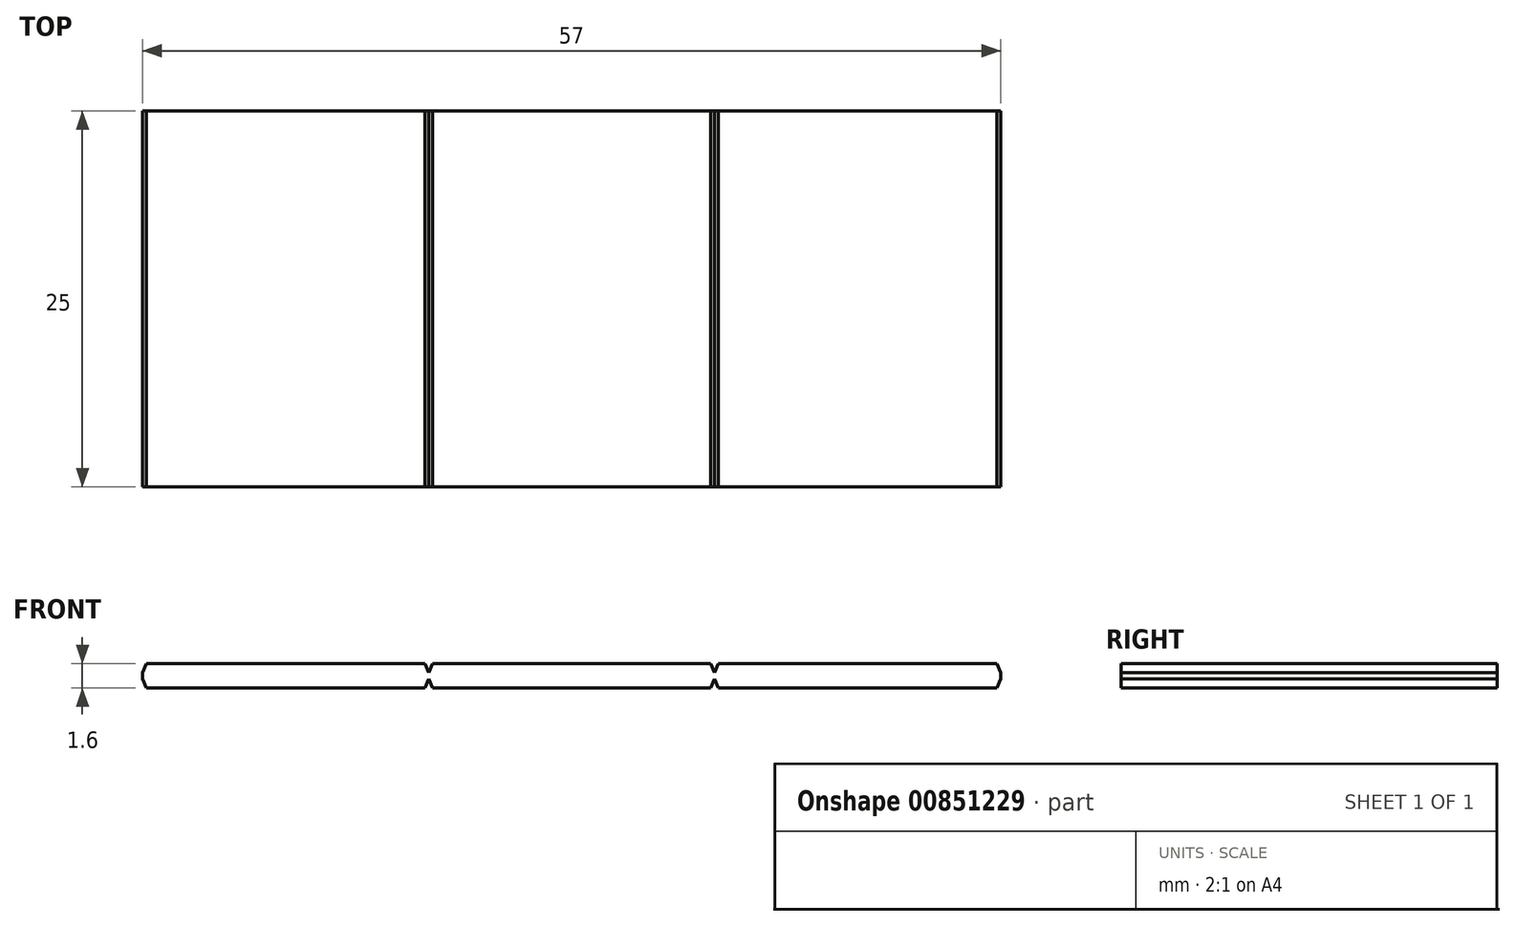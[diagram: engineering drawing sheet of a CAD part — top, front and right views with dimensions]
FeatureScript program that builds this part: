
annotation { "Feature Type Name" : "Feature", "Feature Type Description" : "" }
export const myFeature = defineFeature(function(context is Context, id is Id, definition is map)
    precondition{}
    {
        {
            var Q0;
            Q0=qCreatedBy(makeId("Front.planeOp"),FACE);
            var sketch = newSketch(context, id + "F0", { "sketchPlane" : qUnion([Q0])});
            skLineSegment(sketch, "E0", {"start": v(0, 0.8) * mm, "end": v(-9.25, 0.8) * mm});
            skLineSegment(sketch, "E1", {"start": v(-9.25, 0.8) * mm, "end": v(-9.5, 0.2) * mm});
            skLineSegment(sketch, "E2.MirrorCS", {"start": v(9.25, 0.8) * mm, "end": v(9.5, 0.2) * mm});
            skLineSegment(sketch, "E3.MirrorCS", {"start": v(0, 0.8) * mm, "end": v(9.25, 0.8) * mm});
            skLineSegment(sketch, "E4.MirrorCS", {"start": v(0, -0.8) * mm, "end": v(9.25, -0.8) * mm});
            skLineSegment(sketch, "E5.MirrorCS", {"start": v(-9.25, -0.8) * mm, "end": v(-9.5, -0.2) * mm});
            skLineSegment(sketch, "E6.MirrorCS", {"start": v(0, -0.8) * mm, "end": v(-9.25, -0.8) * mm});
            skLineSegment(sketch, "E7.MirrorCS", {"start": v(9.25, -0.8) * mm, "end": v(9.5, -0.2) * mm});
            skLineSegment(sketch, "E8.1.0.0", {"start": v(19, 0.8) * mm, "end": v(9.75, 0.8) * mm});
            skLineSegment(sketch, "E8.1.0.1", {"start": v(28.25, -0.8) * mm, "end": v(28.5, -0.2) * mm});
            skLineSegment(sketch, "E8.1.0.2", {"start": v(28.25, 0.8) * mm, "end": v(28.5, 0.2) * mm});
            skLineSegment(sketch, "E8.1.0.3", {"start": v(19, -0.8) * mm, "end": v(9.75, -0.8) * mm});
            skLineSegment(sketch, "E8.1.0.4", {"start": v(9.75, 0.8) * mm, "end": v(9.5, 0.2) * mm});
            skLineSegment(sketch, "E8.1.0.5", {"start": v(19, 0.8) * mm, "end": v(28.25, 0.8) * mm});
            skLineSegment(sketch, "E8.1.0.6", {"start": v(9.75, -0.8) * mm, "end": v(9.5, -0.2) * mm});
            skLineSegment(sketch, "E8.1.0.7", {"start": v(19, -0.8) * mm, "end": v(28.25, -0.8) * mm});
            skLineSegment(sketch, "E8.1.0.8", {"start": v(19, 0.8) * mm, "end": v(9.75, 0.8) * mm});
            skLineSegment(sketch, "E8.1.0.9", {"start": v(19, -0.8) * mm, "end": v(28.25, -0.8) * mm});
            skLineSegment(sketch, "E8.1.0.10", {"start": v(28.25, -0.8) * mm, "end": v(28.5, -0.2) * mm});
            skLineSegment(sketch, "E8.1.0.11", {"start": v(9.75, 0.8) * mm, "end": v(9.5, 0.2) * mm});
            skLineSegment(sketch, "E8.1.0.12", {"start": v(19, 0.8) * mm, "end": v(28.25, 0.8) * mm});
            skLineSegment(sketch, "E8.1.0.13", {"start": v(28.25, 0.8) * mm, "end": v(28.5, 0.2) * mm});
            skLineSegment(sketch, "E8.1.0.14", {"start": v(19, -0.8) * mm, "end": v(9.75, -0.8) * mm});
            skLineSegment(sketch, "E8.1.0.15", {"start": v(9.75, -0.8) * mm, "end": v(9.5, -0.2) * mm});
            skLineSegment(sketch, "E8.1.0.16", {"start": v(19, 0.8) * mm, "end": v(9.75, 0.8) * mm});
            skLineSegment(sketch, "E8.1.0.17", {"start": v(9.75, 0.8) * mm, "end": v(9.5, 0.2) * mm});
            skLineSegment(sketch, "E8.1.0.18", {"start": v(28.25, -0.8) * mm, "end": v(28.5, -0.2) * mm});
            skLineSegment(sketch, "E8.1.0.19", {"start": v(19, -0.8) * mm, "end": v(28.25, -0.8) * mm});
            skLineSegment(sketch, "E8.1.0.20", {"start": v(19, -0.8) * mm, "end": v(9.75, -0.8) * mm});
            skLineSegment(sketch, "E8.1.0.21", {"start": v(19, 0.8) * mm, "end": v(28.25, 0.8) * mm});
            skLineSegment(sketch, "E8.1.0.22", {"start": v(28.25, 0.8) * mm, "end": v(28.5, 0.2) * mm});
            skLineSegment(sketch, "E8.1.0.23", {"start": v(9.75, -0.8) * mm, "end": v(9.5, -0.2) * mm});
            skLineSegment(sketch, "E8.1.0.24", {"start": v(19, 0.8) * mm, "end": v(9.75, 0.8) * mm});
            skLineSegment(sketch, "E8.1.0.25", {"start": v(9.75, 0.8) * mm, "end": v(9.5, 0.2) * mm});
            skLineSegment(sketch, "E8.1.0.26", {"start": v(28.25, -0.8) * mm, "end": v(28.5, -0.2) * mm});
            skLineSegment(sketch, "E8.1.0.27", {"start": v(19, -0.8) * mm, "end": v(9.75, -0.8) * mm});
            skLineSegment(sketch, "E8.1.0.28", {"start": v(19, 0.8) * mm, "end": v(28.25, 0.8) * mm});
            skLineSegment(sketch, "E8.1.0.29", {"start": v(19, -0.8) * mm, "end": v(28.25, -0.8) * mm});
            skLineSegment(sketch, "E8.1.0.30", {"start": v(28.25, 0.8) * mm, "end": v(28.5, 0.2) * mm});
            skLineSegment(sketch, "E8.1.0.31", {"start": v(9.75, -0.8) * mm, "end": v(9.5, -0.2) * mm});
            skLineSegment(sketch, "E8.1.0.32", {"start": v(19, 0.8) * mm, "end": v(9.75, 0.8) * mm});
            skLineSegment(sketch, "E8.1.0.33", {"start": v(9.75, 0.8) * mm, "end": v(9.5, 0.2) * mm});
            skLineSegment(sketch, "E8.1.0.34", {"start": v(19, 0.8) * mm, "end": v(28.25, 0.8) * mm});
            skLineSegment(sketch, "E8.1.0.35", {"start": v(19, -0.8) * mm, "end": v(9.75, -0.8) * mm});
            skLineSegment(sketch, "E8.1.0.36", {"start": v(28.25, -0.8) * mm, "end": v(28.5, -0.2) * mm});
            skLineSegment(sketch, "E8.1.0.37", {"start": v(19, -0.8) * mm, "end": v(28.25, -0.8) * mm});
            skLineSegment(sketch, "E8.1.0.38", {"start": v(28.25, 0.8) * mm, "end": v(28.5, 0.2) * mm});
            skLineSegment(sketch, "E8.1.0.39", {"start": v(9.75, -0.8) * mm, "end": v(9.5, -0.2) * mm});
            skLineSegment(sketch, "E8.1.0.40", {"start": v(19, -0.8) * mm, "end": v(28.25, -0.8) * mm});
            skLineSegment(sketch, "E8.1.0.41", {"start": v(19, 0.8) * mm, "end": v(9.75, 0.8) * mm});
            skLineSegment(sketch, "E8.1.0.42", {"start": v(19, -0.8) * mm, "end": v(9.75, -0.8) * mm});
            skLineSegment(sketch, "E8.1.0.43", {"start": v(9.75, 0.8) * mm, "end": v(9.5, 0.2) * mm});
            skLineSegment(sketch, "E8.1.0.44", {"start": v(19, 0.8) * mm, "end": v(28.25, 0.8) * mm});
            skLineSegment(sketch, "E8.1.0.45", {"start": v(28.25, -0.8) * mm, "end": v(28.5, -0.2) * mm});
            skLineSegment(sketch, "E8.1.0.46", {"start": v(9.75, -0.8) * mm, "end": v(9.5, -0.2) * mm});
            skLineSegment(sketch, "E8.1.0.47", {"start": v(28.25, 0.8) * mm, "end": v(28.5, 0.2) * mm});
            skLineSegment(sketch, "E8.1.0.48", {"start": v(19, -0.8) * mm, "end": v(28.25, -0.8) * mm});
            skLineSegment(sketch, "E8.1.0.49", {"start": v(19, 0.8) * mm, "end": v(9.75, 0.8) * mm});
            skLineSegment(sketch, "E8.1.0.50", {"start": v(19, -0.8) * mm, "end": v(9.75, -0.8) * mm});
            skLineSegment(sketch, "E8.1.0.51", {"start": v(28.25, -0.8) * mm, "end": v(28.5, -0.2) * mm});
            skLineSegment(sketch, "E8.1.0.52", {"start": v(9.75, 0.8) * mm, "end": v(9.5, 0.2) * mm});
            skLineSegment(sketch, "E8.1.0.53", {"start": v(9.75, -0.8) * mm, "end": v(9.5, -0.2) * mm});
            skLineSegment(sketch, "E8.1.0.54", {"start": v(19, 0.8) * mm, "end": v(28.25, 0.8) * mm});
            skLineSegment(sketch, "E8.1.0.55", {"start": v(28.25, 0.8) * mm, "end": v(28.5, 0.2) * mm});
            skLineSegment(sketch, "E8.1.0.56", {"start": v(28.25, -0.8) * mm, "end": v(28.5, -0.2) * mm});
            skLineSegment(sketch, "E8.1.0.57", {"start": v(19, -0.8) * mm, "end": v(28.25, -0.8) * mm});
            skLineSegment(sketch, "E8.1.0.58", {"start": v(19, -0.8) * mm, "end": v(9.75, -0.8) * mm});
            skLineSegment(sketch, "E8.1.0.59", {"start": v(19, 0.8) * mm, "end": v(9.75, 0.8) * mm});
            skLineSegment(sketch, "E8.1.0.60", {"start": v(19, 0.8) * mm, "end": v(28.25, 0.8) * mm});
            skLineSegment(sketch, "E8.1.0.61", {"start": v(9.75, 0.8) * mm, "end": v(9.5, 0.2) * mm});
            skLineSegment(sketch, "E8.1.0.62", {"start": v(9.75, -0.8) * mm, "end": v(9.5, -0.2) * mm});
            skLineSegment(sketch, "E8.1.0.63", {"start": v(28.25, 0.8) * mm, "end": v(28.5, 0.2) * mm});
            skLineSegment(sketch, "E8.1.0.64", {"start": v(19, -0.8) * mm, "end": v(28.25, -0.8) * mm});
            skLineSegment(sketch, "E8.1.0.65", {"start": v(19, 0.8) * mm, "end": v(9.75, 0.8) * mm});
            skLineSegment(sketch, "E8.1.0.66", {"start": v(19, -0.8) * mm, "end": v(9.75, -0.8) * mm});
            skLineSegment(sketch, "E8.1.0.67", {"start": v(28.25, 0.8) * mm, "end": v(28.5, 0.2) * mm});
            skLineSegment(sketch, "E8.1.0.68", {"start": v(28.25, -0.8) * mm, "end": v(28.5, -0.2) * mm});
            skLineSegment(sketch, "E8.1.0.69", {"start": v(19, 0.8) * mm, "end": v(28.25, 0.8) * mm});
            skLineSegment(sketch, "E8.1.0.70", {"start": v(9.75, 0.8) * mm, "end": v(9.5, 0.2) * mm});
            skLineSegment(sketch, "E8.1.0.71", {"start": v(9.75, -0.8) * mm, "end": v(9.5, -0.2) * mm});
            skLineSegment(sketch, "E8.1.0.72", {"start": v(19, -0.8) * mm, "end": v(28.25, -0.8) * mm});
            skLineSegment(sketch, "E8.1.0.73", {"start": v(28.25, -0.8) * mm, "end": v(28.5, -0.2) * mm});
            skLineSegment(sketch, "E8.1.0.74", {"start": v(19, -0.8) * mm, "end": v(9.75, -0.8) * mm});
            skLineSegment(sketch, "E8.1.0.75", {"start": v(9.75, 0.8) * mm, "end": v(9.5, 0.2) * mm});
            skLineSegment(sketch, "E8.1.0.76", {"start": v(19, 0.8) * mm, "end": v(9.75, 0.8) * mm});
            skLineSegment(sketch, "E8.1.0.77", {"start": v(28.25, 0.8) * mm, "end": v(28.5, 0.2) * mm});
            skLineSegment(sketch, "E8.1.0.78", {"start": v(19, 0.8) * mm, "end": v(28.25, 0.8) * mm});
            skLineSegment(sketch, "E8.1.0.79", {"start": v(9.75, -0.8) * mm, "end": v(9.5, -0.2) * mm});
            skLineSegment(sketch, "E8.1.0.80", {"start": v(9.75, 0.8) * mm, "end": v(9.5, 0.2) * mm});
            skLineSegment(sketch, "E8.1.0.81", {"start": v(19, 0.8) * mm, "end": v(28.25, 0.8) * mm});
            skLineSegment(sketch, "E8.1.0.82", {"start": v(9.75, -0.8) * mm, "end": v(9.5, -0.2) * mm});
            skLineSegment(sketch, "E8.1.0.83", {"start": v(28.25, -0.8) * mm, "end": v(28.5, -0.2) * mm});
            skLineSegment(sketch, "E8.1.0.84", {"start": v(19, -0.8) * mm, "end": v(9.75, -0.8) * mm});
            skLineSegment(sketch, "E8.1.0.85", {"start": v(19, -0.8) * mm, "end": v(28.25, -0.8) * mm});
            skLineSegment(sketch, "E8.1.0.86", {"start": v(19, 0.8) * mm, "end": v(9.75, 0.8) * mm});
            skLineSegment(sketch, "E8.1.0.87", {"start": v(28.25, 0.8) * mm, "end": v(28.5, 0.2) * mm});
            skLineSegment(sketch, "E8.1.0.88", {"start": v(9.75, 0.8) * mm, "end": v(9.5, 0.2) * mm});
            skLineSegment(sketch, "E8.1.0.89", {"start": v(9.75, -0.8) * mm, "end": v(9.5, -0.2) * mm});
            skLineSegment(sketch, "E8.1.0.90", {"start": v(19, -0.8) * mm, "end": v(28.25, -0.8) * mm});
            skLineSegment(sketch, "E8.1.0.91", {"start": v(28.25, 0.8) * mm, "end": v(28.5, 0.2) * mm});
            skLineSegment(sketch, "E8.1.0.92", {"start": v(19, 0.8) * mm, "end": v(9.75, 0.8) * mm});
            skLineSegment(sketch, "E8.1.0.93", {"start": v(19, -0.8) * mm, "end": v(9.75, -0.8) * mm});
            skLineSegment(sketch, "E8.1.0.94", {"start": v(19, 0.8) * mm, "end": v(28.25, 0.8) * mm});
            skLineSegment(sketch, "E8.1.0.95", {"start": v(28.25, -0.8) * mm, "end": v(28.5, -0.2) * mm});
            skLineSegment(sketch, "E8.1.0.96", {"start": v(28.25, 0.8) * mm, "end": v(28.5, 0.2) * mm});
            skLineSegment(sketch, "E8.1.0.97", {"start": v(19, -0.8) * mm, "end": v(28.25, -0.8) * mm});
            skLineSegment(sketch, "E8.1.0.98", {"start": v(9.75, 0.8) * mm, "end": v(9.5, 0.2) * mm});
            skLineSegment(sketch, "E8.1.0.99", {"start": v(19, 0.8) * mm, "end": v(9.75, 0.8) * mm});
            skLineSegment(sketch, "E8.1.0.100", {"start": v(19, -0.8) * mm, "end": v(9.75, -0.8) * mm});
            skLineSegment(sketch, "E8.1.0.101", {"start": v(19, 0.8) * mm, "end": v(28.25, 0.8) * mm});
            skLineSegment(sketch, "E8.1.0.102", {"start": v(28.25, -0.8) * mm, "end": v(28.5, -0.2) * mm});
            skLineSegment(sketch, "E8.1.0.103", {"start": v(9.75, -0.8) * mm, "end": v(9.5, -0.2) * mm});
            skLineSegment(sketch, "E8.1.0.104", {"start": v(19, -0.8) * mm, "end": v(9.75, -0.8) * mm});
            skLineSegment(sketch, "E8.1.0.105", {"start": v(19, 0.8) * mm, "end": v(28.25, 0.8) * mm});
            skLineSegment(sketch, "E8.1.0.106", {"start": v(28.25, 0.8) * mm, "end": v(28.5, 0.2) * mm});
            skLineSegment(sketch, "E8.1.0.107", {"start": v(28.25, -0.8) * mm, "end": v(28.5, -0.2) * mm});
            skLineSegment(sketch, "E8.1.0.108", {"start": v(9.75, -0.8) * mm, "end": v(9.5, -0.2) * mm});
            skLineSegment(sketch, "E8.1.0.109", {"start": v(9.75, 0.8) * mm, "end": v(9.5, 0.2) * mm});
            skLineSegment(sketch, "E8.1.0.110", {"start": v(19, 0.8) * mm, "end": v(9.75, 0.8) * mm});
            skLineSegment(sketch, "E8.1.0.111", {"start": v(19, -0.8) * mm, "end": v(28.25, -0.8) * mm});
            skLineSegment(sketch, "E8.1.0.112", {"start": v(28.25, -0.8) * mm, "end": v(28.5, -0.2) * mm});
            skLineSegment(sketch, "E8.1.0.113", {"start": v(19, 0.8) * mm, "end": v(28.25, 0.8) * mm});
            skLineSegment(sketch, "E8.1.0.114", {"start": v(28.25, 0.8) * mm, "end": v(28.5, 0.2) * mm});
            skLineSegment(sketch, "E8.1.0.115", {"start": v(9.75, -0.8) * mm, "end": v(9.5, -0.2) * mm});
            skLineSegment(sketch, "E8.1.0.116", {"start": v(9.75, 0.8) * mm, "end": v(9.5, 0.2) * mm});
            skLineSegment(sketch, "E8.1.0.117", {"start": v(19, -0.8) * mm, "end": v(9.75, -0.8) * mm});
            skLineSegment(sketch, "E8.1.0.118", {"start": v(19, -0.8) * mm, "end": v(28.25, -0.8) * mm});
            skLineSegment(sketch, "E8.1.0.119", {"start": v(19, 0.8) * mm, "end": v(9.75, 0.8) * mm});
            skLineSegment(sketch, "E8.1.0.120", {"start": v(28.25, 0.8) * mm, "end": v(28.5, 0.2) * mm});
            skLineSegment(sketch, "E8.1.0.121", {"start": v(9.75, -0.8) * mm, "end": v(9.5, -0.2) * mm});
            skLineSegment(sketch, "E8.1.0.122", {"start": v(19, 0.8) * mm, "end": v(9.75, 0.8) * mm});
            skLineSegment(sketch, "E8.1.0.123", {"start": v(19, -0.8) * mm, "end": v(28.25, -0.8) * mm});
            skLineSegment(sketch, "E8.1.0.124", {"start": v(19, -0.8) * mm, "end": v(9.75, -0.8) * mm});
            skLineSegment(sketch, "E8.1.0.125", {"start": v(19, 0.8) * mm, "end": v(28.25, 0.8) * mm});
            skLineSegment(sketch, "E8.1.0.126", {"start": v(9.75, 0.8) * mm, "end": v(9.5, 0.2) * mm});
            skLineSegment(sketch, "E8.1.0.127", {"start": v(28.25, -0.8) * mm, "end": v(28.5, -0.2) * mm});
            skLineSegment(sketch, "E8.2.0.0", {"start": v(38, 0.8) * mm, "end": v(28.75, 0.8) * mm});
            skLineSegment(sketch, "E8.2.0.1", {"start": v(47.25, -0.8) * mm, "end": v(47.5, -0.2) * mm});
            skLineSegment(sketch, "E8.2.0.2", {"start": v(47.25, 0.8) * mm, "end": v(47.5, 0.2) * mm});
            skLineSegment(sketch, "E8.2.0.3", {"start": v(38, -0.8) * mm, "end": v(28.75, -0.8) * mm});
            skLineSegment(sketch, "E8.2.0.4", {"start": v(28.75, 0.8) * mm, "end": v(28.5, 0.2) * mm});
            skLineSegment(sketch, "E8.2.0.5", {"start": v(38, 0.8) * mm, "end": v(47.25, 0.8) * mm});
            skLineSegment(sketch, "E8.2.0.6", {"start": v(28.75, -0.8) * mm, "end": v(28.5, -0.2) * mm});
            skLineSegment(sketch, "E8.2.0.7", {"start": v(38, -0.8) * mm, "end": v(47.25, -0.8) * mm});
            skLineSegment(sketch, "E8.2.0.8", {"start": v(38, 0.8) * mm, "end": v(28.75, 0.8) * mm});
            skLineSegment(sketch, "E8.2.0.9", {"start": v(38, -0.8) * mm, "end": v(47.25, -0.8) * mm});
            skLineSegment(sketch, "E8.2.0.10", {"start": v(47.25, -0.8) * mm, "end": v(47.5, -0.2) * mm});
            skLineSegment(sketch, "E8.2.0.11", {"start": v(28.75, 0.8) * mm, "end": v(28.5, 0.2) * mm});
            skLineSegment(sketch, "E8.2.0.12", {"start": v(38, 0.8) * mm, "end": v(47.25, 0.8) * mm});
            skLineSegment(sketch, "E8.2.0.13", {"start": v(47.25, 0.8) * mm, "end": v(47.5, 0.2) * mm});
            skLineSegment(sketch, "E8.2.0.14", {"start": v(38, -0.8) * mm, "end": v(28.75, -0.8) * mm});
            skLineSegment(sketch, "E8.2.0.15", {"start": v(28.75, -0.8) * mm, "end": v(28.5, -0.2) * mm});
            skLineSegment(sketch, "E8.2.0.16", {"start": v(38, 0.8) * mm, "end": v(28.75, 0.8) * mm});
            skLineSegment(sketch, "E8.2.0.17", {"start": v(28.75, 0.8) * mm, "end": v(28.5, 0.2) * mm});
            skLineSegment(sketch, "E8.2.0.18", {"start": v(47.25, -0.8) * mm, "end": v(47.5, -0.2) * mm});
            skLineSegment(sketch, "E8.2.0.19", {"start": v(38, -0.8) * mm, "end": v(47.25, -0.8) * mm});
            skLineSegment(sketch, "E8.2.0.20", {"start": v(38, -0.8) * mm, "end": v(28.75, -0.8) * mm});
            skLineSegment(sketch, "E8.2.0.21", {"start": v(38, 0.8) * mm, "end": v(47.25, 0.8) * mm});
            skLineSegment(sketch, "E8.2.0.22", {"start": v(47.25, 0.8) * mm, "end": v(47.5, 0.2) * mm});
            skLineSegment(sketch, "E8.2.0.23", {"start": v(28.75, -0.8) * mm, "end": v(28.5, -0.2) * mm});
            skLineSegment(sketch, "E8.2.0.24", {"start": v(38, 0.8) * mm, "end": v(28.75, 0.8) * mm});
            skLineSegment(sketch, "E8.2.0.25", {"start": v(28.75, 0.8) * mm, "end": v(28.5, 0.2) * mm});
            skLineSegment(sketch, "E8.2.0.26", {"start": v(47.25, -0.8) * mm, "end": v(47.5, -0.2) * mm});
            skLineSegment(sketch, "E8.2.0.27", {"start": v(38, -0.8) * mm, "end": v(28.75, -0.8) * mm});
            skLineSegment(sketch, "E8.2.0.28", {"start": v(38, 0.8) * mm, "end": v(47.25, 0.8) * mm});
            skLineSegment(sketch, "E8.2.0.29", {"start": v(38, -0.8) * mm, "end": v(47.25, -0.8) * mm});
            skLineSegment(sketch, "E8.2.0.30", {"start": v(47.25, 0.8) * mm, "end": v(47.5, 0.2) * mm});
            skLineSegment(sketch, "E8.2.0.31", {"start": v(28.75, -0.8) * mm, "end": v(28.5, -0.2) * mm});
            skLineSegment(sketch, "E8.2.0.32", {"start": v(38, 0.8) * mm, "end": v(28.75, 0.8) * mm});
            skLineSegment(sketch, "E8.2.0.33", {"start": v(28.75, 0.8) * mm, "end": v(28.5, 0.2) * mm});
            skLineSegment(sketch, "E8.2.0.34", {"start": v(38, 0.8) * mm, "end": v(47.25, 0.8) * mm});
            skLineSegment(sketch, "E8.2.0.35", {"start": v(38, -0.8) * mm, "end": v(28.75, -0.8) * mm});
            skLineSegment(sketch, "E8.2.0.36", {"start": v(47.25, -0.8) * mm, "end": v(47.5, -0.2) * mm});
            skLineSegment(sketch, "E8.2.0.37", {"start": v(38, -0.8) * mm, "end": v(47.25, -0.8) * mm});
            skLineSegment(sketch, "E8.2.0.38", {"start": v(47.25, 0.8) * mm, "end": v(47.5, 0.2) * mm});
            skLineSegment(sketch, "E8.2.0.39", {"start": v(28.75, -0.8) * mm, "end": v(28.5, -0.2) * mm});
            skLineSegment(sketch, "E8.2.0.40", {"start": v(38, -0.8) * mm, "end": v(47.25, -0.8) * mm});
            skLineSegment(sketch, "E8.2.0.41", {"start": v(38, 0.8) * mm, "end": v(28.75, 0.8) * mm});
            skLineSegment(sketch, "E8.2.0.42", {"start": v(38, -0.8) * mm, "end": v(28.75, -0.8) * mm});
            skLineSegment(sketch, "E8.2.0.43", {"start": v(28.75, 0.8) * mm, "end": v(28.5, 0.2) * mm});
            skLineSegment(sketch, "E8.2.0.44", {"start": v(38, 0.8) * mm, "end": v(47.25, 0.8) * mm});
            skLineSegment(sketch, "E8.2.0.45", {"start": v(47.25, -0.8) * mm, "end": v(47.5, -0.2) * mm});
            skLineSegment(sketch, "E8.2.0.46", {"start": v(28.75, -0.8) * mm, "end": v(28.5, -0.2) * mm});
            skLineSegment(sketch, "E8.2.0.47", {"start": v(47.25, 0.8) * mm, "end": v(47.5, 0.2) * mm});
            skLineSegment(sketch, "E8.2.0.48", {"start": v(38, -0.8) * mm, "end": v(47.25, -0.8) * mm});
            skLineSegment(sketch, "E8.2.0.49", {"start": v(38, 0.8) * mm, "end": v(28.75, 0.8) * mm});
            skLineSegment(sketch, "E8.2.0.50", {"start": v(38, -0.8) * mm, "end": v(28.75, -0.8) * mm});
            skLineSegment(sketch, "E8.2.0.51", {"start": v(47.25, -0.8) * mm, "end": v(47.5, -0.2) * mm});
            skLineSegment(sketch, "E8.2.0.52", {"start": v(28.75, 0.8) * mm, "end": v(28.5, 0.2) * mm});
            skLineSegment(sketch, "E8.2.0.53", {"start": v(28.75, -0.8) * mm, "end": v(28.5, -0.2) * mm});
            skLineSegment(sketch, "E8.2.0.54", {"start": v(38, 0.8) * mm, "end": v(47.25, 0.8) * mm});
            skLineSegment(sketch, "E8.2.0.55", {"start": v(47.25, 0.8) * mm, "end": v(47.5, 0.2) * mm});
            skLineSegment(sketch, "E8.2.0.56", {"start": v(47.25, -0.8) * mm, "end": v(47.5, -0.2) * mm});
            skLineSegment(sketch, "E8.2.0.57", {"start": v(38, -0.8) * mm, "end": v(47.25, -0.8) * mm});
            skLineSegment(sketch, "E8.2.0.58", {"start": v(38, -0.8) * mm, "end": v(28.75, -0.8) * mm});
            skLineSegment(sketch, "E8.2.0.59", {"start": v(38, 0.8) * mm, "end": v(28.75, 0.8) * mm});
            skLineSegment(sketch, "E8.2.0.60", {"start": v(38, 0.8) * mm, "end": v(47.25, 0.8) * mm});
            skLineSegment(sketch, "E8.2.0.61", {"start": v(28.75, 0.8) * mm, "end": v(28.5, 0.2) * mm});
            skLineSegment(sketch, "E8.2.0.62", {"start": v(28.75, -0.8) * mm, "end": v(28.5, -0.2) * mm});
            skLineSegment(sketch, "E8.2.0.63", {"start": v(47.25, 0.8) * mm, "end": v(47.5, 0.2) * mm});
            skLineSegment(sketch, "E8.2.0.64", {"start": v(38, -0.8) * mm, "end": v(47.25, -0.8) * mm});
            skLineSegment(sketch, "E8.2.0.65", {"start": v(38, 0.8) * mm, "end": v(28.75, 0.8) * mm});
            skLineSegment(sketch, "E8.2.0.66", {"start": v(38, -0.8) * mm, "end": v(28.75, -0.8) * mm});
            skLineSegment(sketch, "E8.2.0.67", {"start": v(47.25, 0.8) * mm, "end": v(47.5, 0.2) * mm});
            skLineSegment(sketch, "E8.2.0.68", {"start": v(47.25, -0.8) * mm, "end": v(47.5, -0.2) * mm});
            skLineSegment(sketch, "E8.2.0.69", {"start": v(38, 0.8) * mm, "end": v(47.25, 0.8) * mm});
            skLineSegment(sketch, "E8.2.0.70", {"start": v(28.75, 0.8) * mm, "end": v(28.5, 0.2) * mm});
            skLineSegment(sketch, "E8.2.0.71", {"start": v(28.75, -0.8) * mm, "end": v(28.5, -0.2) * mm});
            skLineSegment(sketch, "E8.2.0.72", {"start": v(38, -0.8) * mm, "end": v(47.25, -0.8) * mm});
            skLineSegment(sketch, "E8.2.0.73", {"start": v(47.25, -0.8) * mm, "end": v(47.5, -0.2) * mm});
            skLineSegment(sketch, "E8.2.0.74", {"start": v(38, -0.8) * mm, "end": v(28.75, -0.8) * mm});
            skLineSegment(sketch, "E8.2.0.75", {"start": v(28.75, 0.8) * mm, "end": v(28.5, 0.2) * mm});
            skLineSegment(sketch, "E8.2.0.76", {"start": v(38, 0.8) * mm, "end": v(28.75, 0.8) * mm});
            skLineSegment(sketch, "E8.2.0.77", {"start": v(47.25, 0.8) * mm, "end": v(47.5, 0.2) * mm});
            skLineSegment(sketch, "E8.2.0.78", {"start": v(38, 0.8) * mm, "end": v(47.25, 0.8) * mm});
            skLineSegment(sketch, "E8.2.0.79", {"start": v(28.75, -0.8) * mm, "end": v(28.5, -0.2) * mm});
            skLineSegment(sketch, "E8.2.0.80", {"start": v(28.75, 0.8) * mm, "end": v(28.5, 0.2) * mm});
            skLineSegment(sketch, "E8.2.0.81", {"start": v(38, 0.8) * mm, "end": v(47.25, 0.8) * mm});
            skLineSegment(sketch, "E8.2.0.82", {"start": v(28.75, -0.8) * mm, "end": v(28.5, -0.2) * mm});
            skLineSegment(sketch, "E8.2.0.83", {"start": v(47.25, -0.8) * mm, "end": v(47.5, -0.2) * mm});
            skLineSegment(sketch, "E8.2.0.84", {"start": v(38, -0.8) * mm, "end": v(28.75, -0.8) * mm});
            skLineSegment(sketch, "E8.2.0.85", {"start": v(38, -0.8) * mm, "end": v(47.25, -0.8) * mm});
            skLineSegment(sketch, "E8.2.0.86", {"start": v(38, 0.8) * mm, "end": v(28.75, 0.8) * mm});
            skLineSegment(sketch, "E8.2.0.87", {"start": v(47.25, 0.8) * mm, "end": v(47.5, 0.2) * mm});
            skLineSegment(sketch, "E8.2.0.88", {"start": v(28.75, 0.8) * mm, "end": v(28.5, 0.2) * mm});
            skLineSegment(sketch, "E8.2.0.89", {"start": v(28.75, -0.8) * mm, "end": v(28.5, -0.2) * mm});
            skLineSegment(sketch, "E8.2.0.90", {"start": v(38, -0.8) * mm, "end": v(47.25, -0.8) * mm});
            skLineSegment(sketch, "E8.2.0.91", {"start": v(47.25, 0.8) * mm, "end": v(47.5, 0.2) * mm});
            skLineSegment(sketch, "E8.2.0.92", {"start": v(38, 0.8) * mm, "end": v(28.75, 0.8) * mm});
            skLineSegment(sketch, "E8.2.0.93", {"start": v(38, -0.8) * mm, "end": v(28.75, -0.8) * mm});
            skLineSegment(sketch, "E8.2.0.94", {"start": v(38, 0.8) * mm, "end": v(47.25, 0.8) * mm});
            skLineSegment(sketch, "E8.2.0.95", {"start": v(47.25, -0.8) * mm, "end": v(47.5, -0.2) * mm});
            skLineSegment(sketch, "E8.2.0.96", {"start": v(47.25, 0.8) * mm, "end": v(47.5, 0.2) * mm});
            skLineSegment(sketch, "E8.2.0.97", {"start": v(38, -0.8) * mm, "end": v(47.25, -0.8) * mm});
            skLineSegment(sketch, "E8.2.0.98", {"start": v(28.75, 0.8) * mm, "end": v(28.5, 0.2) * mm});
            skLineSegment(sketch, "E8.2.0.99", {"start": v(38, 0.8) * mm, "end": v(28.75, 0.8) * mm});
            skLineSegment(sketch, "E8.2.0.100", {"start": v(38, -0.8) * mm, "end": v(28.75, -0.8) * mm});
            skLineSegment(sketch, "E8.2.0.101", {"start": v(38, 0.8) * mm, "end": v(47.25, 0.8) * mm});
            skLineSegment(sketch, "E8.2.0.102", {"start": v(47.25, -0.8) * mm, "end": v(47.5, -0.2) * mm});
            skLineSegment(sketch, "E8.2.0.103", {"start": v(28.75, -0.8) * mm, "end": v(28.5, -0.2) * mm});
            skLineSegment(sketch, "E8.2.0.104", {"start": v(38, -0.8) * mm, "end": v(28.75, -0.8) * mm});
            skLineSegment(sketch, "E8.2.0.105", {"start": v(38, 0.8) * mm, "end": v(47.25, 0.8) * mm});
            skLineSegment(sketch, "E8.2.0.106", {"start": v(47.25, 0.8) * mm, "end": v(47.5, 0.2) * mm});
            skLineSegment(sketch, "E8.2.0.107", {"start": v(47.25, -0.8) * mm, "end": v(47.5, -0.2) * mm});
            skLineSegment(sketch, "E8.2.0.108", {"start": v(28.75, -0.8) * mm, "end": v(28.5, -0.2) * mm});
            skLineSegment(sketch, "E8.2.0.109", {"start": v(28.75, 0.8) * mm, "end": v(28.5, 0.2) * mm});
            skLineSegment(sketch, "E8.2.0.110", {"start": v(38, 0.8) * mm, "end": v(28.75, 0.8) * mm});
            skLineSegment(sketch, "E8.2.0.111", {"start": v(38, -0.8) * mm, "end": v(47.25, -0.8) * mm});
            skLineSegment(sketch, "E8.2.0.112", {"start": v(47.25, -0.8) * mm, "end": v(47.5, -0.2) * mm});
            skLineSegment(sketch, "E8.2.0.113", {"start": v(38, 0.8) * mm, "end": v(47.25, 0.8) * mm});
            skLineSegment(sketch, "E8.2.0.114", {"start": v(47.25, 0.8) * mm, "end": v(47.5, 0.2) * mm});
            skLineSegment(sketch, "E8.2.0.115", {"start": v(28.75, -0.8) * mm, "end": v(28.5, -0.2) * mm});
            skLineSegment(sketch, "E8.2.0.116", {"start": v(28.75, 0.8) * mm, "end": v(28.5, 0.2) * mm});
            skLineSegment(sketch, "E8.2.0.117", {"start": v(38, -0.8) * mm, "end": v(28.75, -0.8) * mm});
            skLineSegment(sketch, "E8.2.0.118", {"start": v(38, -0.8) * mm, "end": v(47.25, -0.8) * mm});
            skLineSegment(sketch, "E8.2.0.119", {"start": v(38, 0.8) * mm, "end": v(28.75, 0.8) * mm});
            skLineSegment(sketch, "E8.2.0.120", {"start": v(47.25, 0.8) * mm, "end": v(47.5, 0.2) * mm});
            skLineSegment(sketch, "E8.2.0.121", {"start": v(28.75, -0.8) * mm, "end": v(28.5, -0.2) * mm});
            skLineSegment(sketch, "E8.2.0.122", {"start": v(38, 0.8) * mm, "end": v(28.75, 0.8) * mm});
            skLineSegment(sketch, "E8.2.0.123", {"start": v(38, -0.8) * mm, "end": v(47.25, -0.8) * mm});
            skLineSegment(sketch, "E8.2.0.124", {"start": v(38, -0.8) * mm, "end": v(28.75, -0.8) * mm});
            skLineSegment(sketch, "E8.2.0.125", {"start": v(38, 0.8) * mm, "end": v(47.25, 0.8) * mm});
            skLineSegment(sketch, "E8.2.0.126", {"start": v(28.75, 0.8) * mm, "end": v(28.5, 0.2) * mm});
            skLineSegment(sketch, "E8.2.0.127", {"start": v(47.25, -0.8) * mm, "end": v(47.5, -0.2) * mm});
            skLineSegment(sketch, "E8.direction1", {"start": v(-9.25, -0.8) * mm, "end": v(9.75, -0.8) * mm, "construction": true});
            skLineSegment(sketch, "E9", {"start": v(-9.5, 0.2) * mm, "end": v(-9.5, -0.2) * mm});
            skLineSegment(sketch, "E10", {"start": v(47.5, 0.2) * mm, "end": v(47.5, -0.2) * mm});
            skSolve(sketch);
        }
        {
            var Q0;
            Q0=makeQuery(id+"F0.imprint","IMPRINT",FACE,{"disambiguationData":[TD([[makeQuery(id+"F0.imprint","IMPRINT",EDGE,{"derivedFrom":sQuery(id+"F0.wireOp",EDGE,"E1")}),1.0]])]});
            extrude(context, id + "F1", {"entities" : qUnion([Q0]), "depth" : 25 * mm, "offsetDistance" : 25 * mm});
        }
    });
